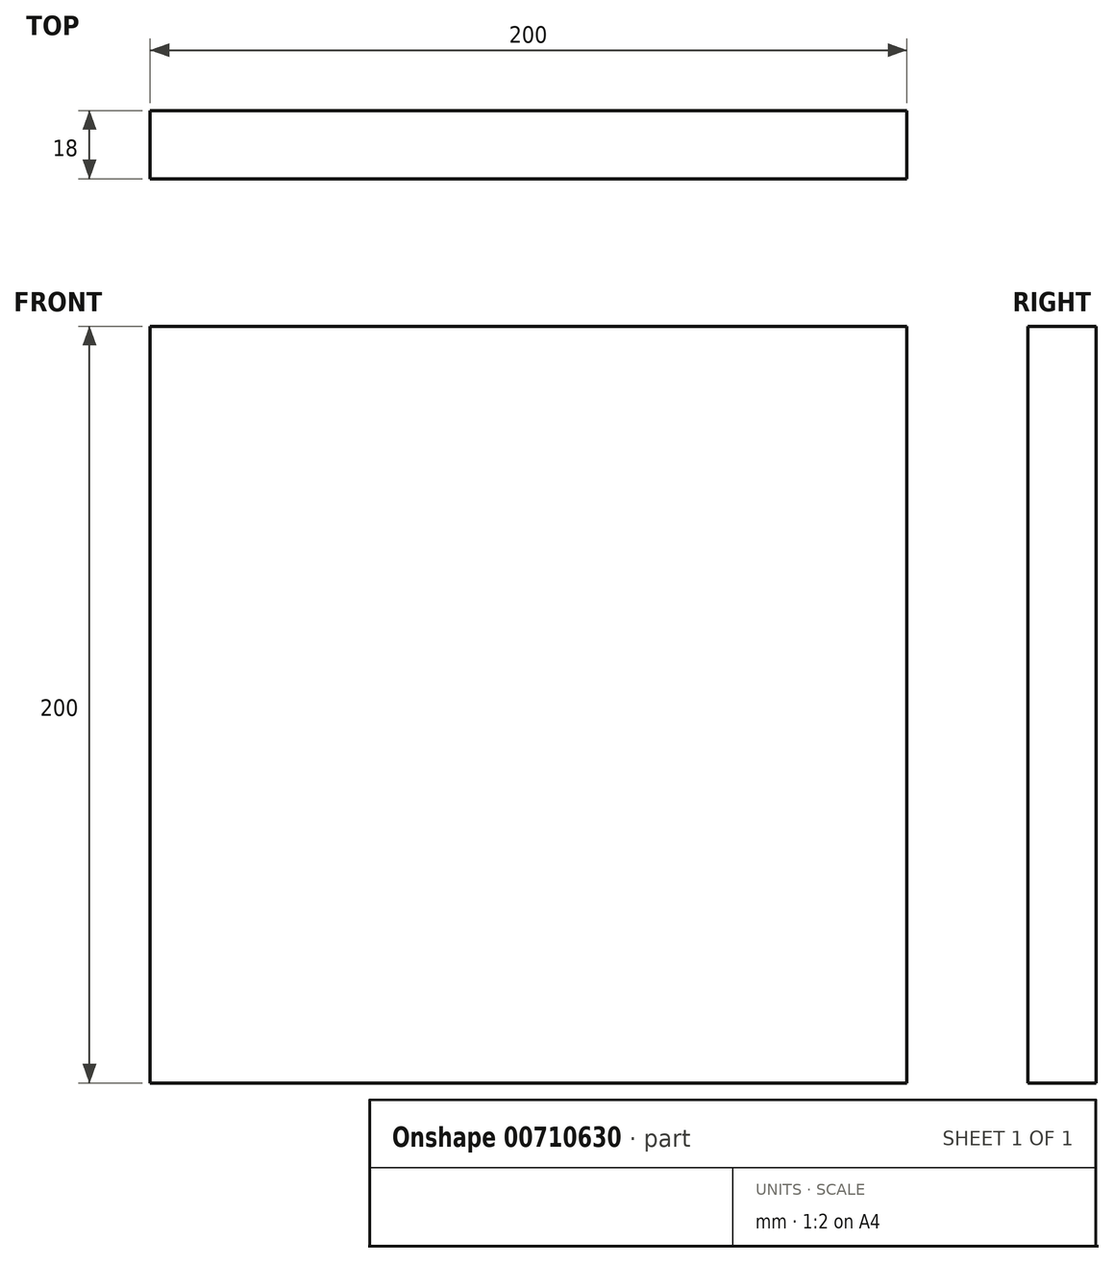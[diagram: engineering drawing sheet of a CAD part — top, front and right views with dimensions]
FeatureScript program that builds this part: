
annotation { "Feature Type Name" : "Feature", "Feature Type Description" : "" }
export const myFeature = defineFeature(function(context is Context, id is Id, definition is map)
    precondition{}
    {
        {
            var Q0;
            Q0=qCreatedBy(makeId("Front.planeOp"),FACE);
            var sketch = newSketch(context, id + "F0", { "sketchPlane" : qUnion([Q0])});
            skLineSegment(sketch, "E0.bottom", {"start": v(4.4, 0) * mm, "end": v(204.4, 0) * mm});
            skLineSegment(sketch, "E0.top", {"start": v(4.4, 200) * mm, "end": v(204.4, 200) * mm});
            skLineSegment(sketch, "E0.left", {"start": v(4.4, 0) * mm, "end": v(4.4, 200) * mm});
            skLineSegment(sketch, "E0.right", {"start": v(204.4, 0) * mm, "end": v(204.4, 200) * mm});
            skSolve(sketch);
        }
        {
            var Q0;
            Q0=makeQuery(id+"F0.imprint","IMPRINT",FACE,{"disambiguationData":[TD([[makeQuery(id+"F0.imprint","IMPRINT",EDGE,{"derivedFrom":sQuery(id+"F0.wireOp",EDGE,"E0.bottom")}),1.0]])]});
            extrude(context, id + "F1", {"entities" : qUnion([Q0]), "depth" : 18 * mm, "offsetDistance" : 25 * mm});
        }
    });
